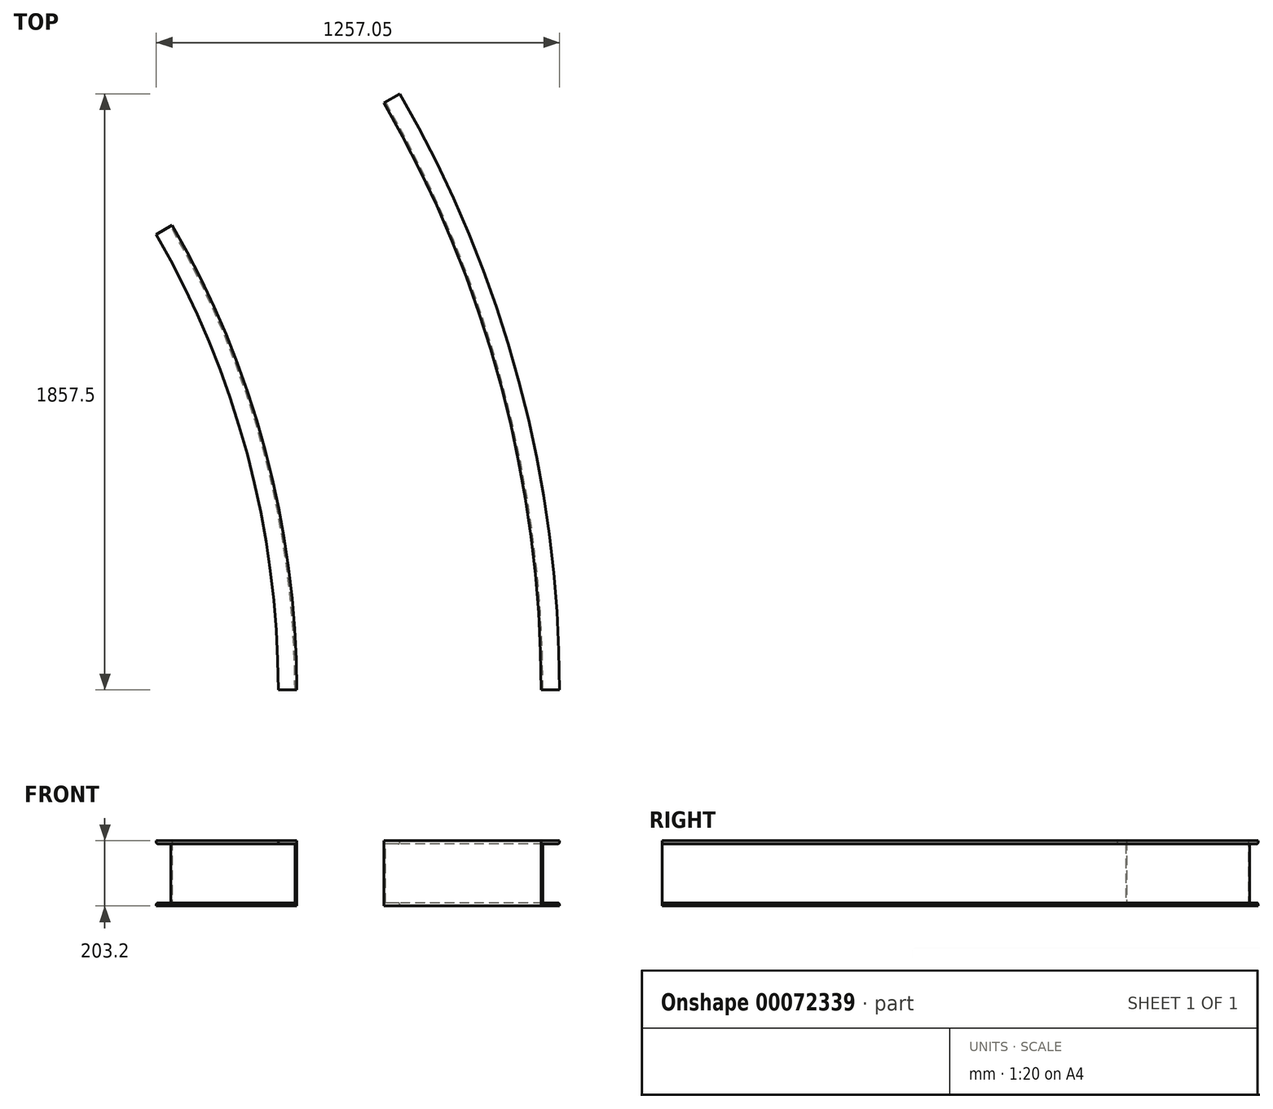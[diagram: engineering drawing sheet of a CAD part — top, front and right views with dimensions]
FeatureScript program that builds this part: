
annotation { "Feature Type Name" : "Feature", "Feature Type Description" : "" }
export const myFeature = defineFeature(function(context is Context, id is Id, definition is map)
    precondition{}
    {
        {
            var Q0;
            Q0=qCreatedBy(makeId("Front.planeOp"),FACE);
            var sketch = newSketch(context, id + "F0", { "sketchPlane" : qUnion([Q0])});
            skLineSegment(sketch, "E0", {"start": v(0, 0) * mm, "end": v(0, -101.6) * mm});
            skLineSegment(sketch, "E1", {"start": v(0, -101.6) * mm, "end": v(57.4, -101.6) * mm});
            skLineSegment(sketch, "E2", {"start": v(57.4, -101.6) * mm, "end": v(57.4, -98.04) * mm});
            skLineSegment(sketch, "E3", {"start": v(51.05, -91.7) * mm, "end": v(5.59, -91.7) * mm});
            skLineSegment(sketch, "E4", {"start": v(5.59, -91.7) * mm, "end": v(5.59, 0) * mm});
            skPoint(sketch, "E5.orphan", {"position": v(0, 109.54) * mm});
            skLineSegment(sketch, "E6.MirrorCS", {"start": v(5.59, 91.7) * mm, "end": v(5.59, 0) * mm});
            skLineSegment(sketch, "E7.MirrorCS", {"start": v(51.05, 91.7) * mm, "end": v(5.59, 91.7) * mm});
            skLineSegment(sketch, "E8.MirrorCS", {"start": v(57.4, 101.6) * mm, "end": v(57.4, 98.04) * mm});
            skLineSegment(sketch, "E9.MirrorCS", {"start": v(0, 101.6) * mm, "end": v(57.4, 101.6) * mm});
            skLineSegment(sketch, "E10.MirrorCS", {"start": v(0, 0) * mm, "end": v(0, 101.6) * mm});
            skPoint(sketch, "E11.visualSharp", {"position": v(57.4, -91.7) * mm});
            skArc(sketch, "E11.filletArc", {"start": v(57.4, -98.04) * mm, "mid": v(55.54, -93.55) * mm, "end": v(51.05, -91.7) * mm});
            skPoint(sketch, "E12.visualSharp", {"position": v(57.4, 91.7) * mm});
            skArc(sketch, "E12.filletArc", {"start": v(51.05, 91.7) * mm, "mid": v(55.54, 93.55) * mm, "end": v(57.4, 98.04) * mm});
            skLineSegment(sketch, "E13", {"start": v(0, 0) * mm, "end": v(-381, 0) * mm});
            skLineSegment(sketch, "E14", {"start": v(-381, 72.29) * mm, "end": v(-381, -111.5) * mm});
            skLineSegment(sketch, "E15.MirrorCS", {"start": v(-762, 101.6) * mm, "end": v(-819.4, 101.6) * mm});
            skLineSegment(sketch, "E16.MirrorCS", {"start": v(-813.05, 91.7) * mm, "end": v(-767.59, 91.7) * mm});
            skLineSegment(sketch, "E17.MirrorCS", {"start": v(-762, 0) * mm, "end": v(-762, 101.6) * mm});
            skLineSegment(sketch, "E18.MirrorCS", {"start": v(-767.59, 91.7) * mm, "end": v(-767.59, 0) * mm});
            skLineSegment(sketch, "E19.MirrorCS", {"start": v(-819.4, 101.6) * mm, "end": v(-819.4, 98.04) * mm});
            skArc(sketch, "E20.MirrorCS", {"start": v(-813.05, 91.7) * mm, "mid": v(-817.54, 93.55) * mm, "end": v(-819.4, 98.04) * mm});
            skLineSegment(sketch, "E21.MirrorCS", {"start": v(-762, 0) * mm, "end": v(-762, -101.6) * mm});
            skLineSegment(sketch, "E22.MirrorCS", {"start": v(-762, -101.6) * mm, "end": v(-819.4, -101.6) * mm});
            skLineSegment(sketch, "E23.MirrorCS", {"start": v(-813.05, -91.7) * mm, "end": v(-767.59, -91.7) * mm});
            skLineSegment(sketch, "E24.MirrorCS", {"start": v(-767.59, -91.7) * mm, "end": v(-767.59, 0) * mm});
            skArc(sketch, "E25.MirrorCS", {"start": v(-819.4, -98.04) * mm, "mid": v(-817.54, -93.55) * mm, "end": v(-813.05, -91.7) * mm});
            skLineSegment(sketch, "E26.MirrorCS", {"start": v(-819.4, -101.6) * mm, "end": v(-819.4, -98.04) * mm});
            skSolve(sketch);
        }
        {
            var Q0;
            Q0=qCreatedBy(makeId("Top.planeOp"),FACE);
            var sketch = newSketch(context, id + "F1", { "sketchPlane" : qUnion([Q0])});
            skArc(sketch, "E27", {"start": v(0, 0) * mm, "mid": v(-124.63, 946.66) * mm, "end": v(-490.03, 1828.8) * mm});
            skArc(sketch, "E28", {"start": v(-762, 0) * mm, "mid": v(-860.67, 749.44) * mm, "end": v(-1149.94, 1447.8) * mm});
            skLineSegment(sketch, "E29", {"start": v(-762, 0) * mm, "end": v(0, 0) * mm});
            skLineSegment(sketch, "E30", {"start": v(-1149.94, 1447.8) * mm, "end": v(-490.03, 1828.8) * mm});
            skSolve(sketch);
        }
        {
            var Q0;
            Q0=makeQuery(id+"F0.imprint","IMPRINT",FACE,{"disambiguationData":[TD([[makeQuery(id+"F0.imprint","IMPRINT",EDGE,{"derivedFrom":sQuery(id+"F0.wireOp",EDGE,"E0")}),1.0]])]});
            var Q1;
            Q1=sQuery(id+"F1.wireOp",EDGE,"E27");
            sweep(context, id + "F2", {"profiles" : qUnion([Q0]), "path" : qUnion([Q1])});
        }
        {
            var Q0;
            Q0=makeQuery(id+"F0.imprint","IMPRINT",FACE,{"disambiguationData":[TD([[makeQuery(id+"F0.imprint","IMPRINT",EDGE,{"derivedFrom":sQuery(id+"F0.wireOp",EDGE,"E15.MirrorCS")}),1.0]])]});
            var Q1;
            Q1=sQuery(id+"F1.wireOp",EDGE,"E28");
            sweep(context, id + "F3", {"profiles" : qUnion([Q0]), "path" : qUnion([Q1])});
        }
    });
